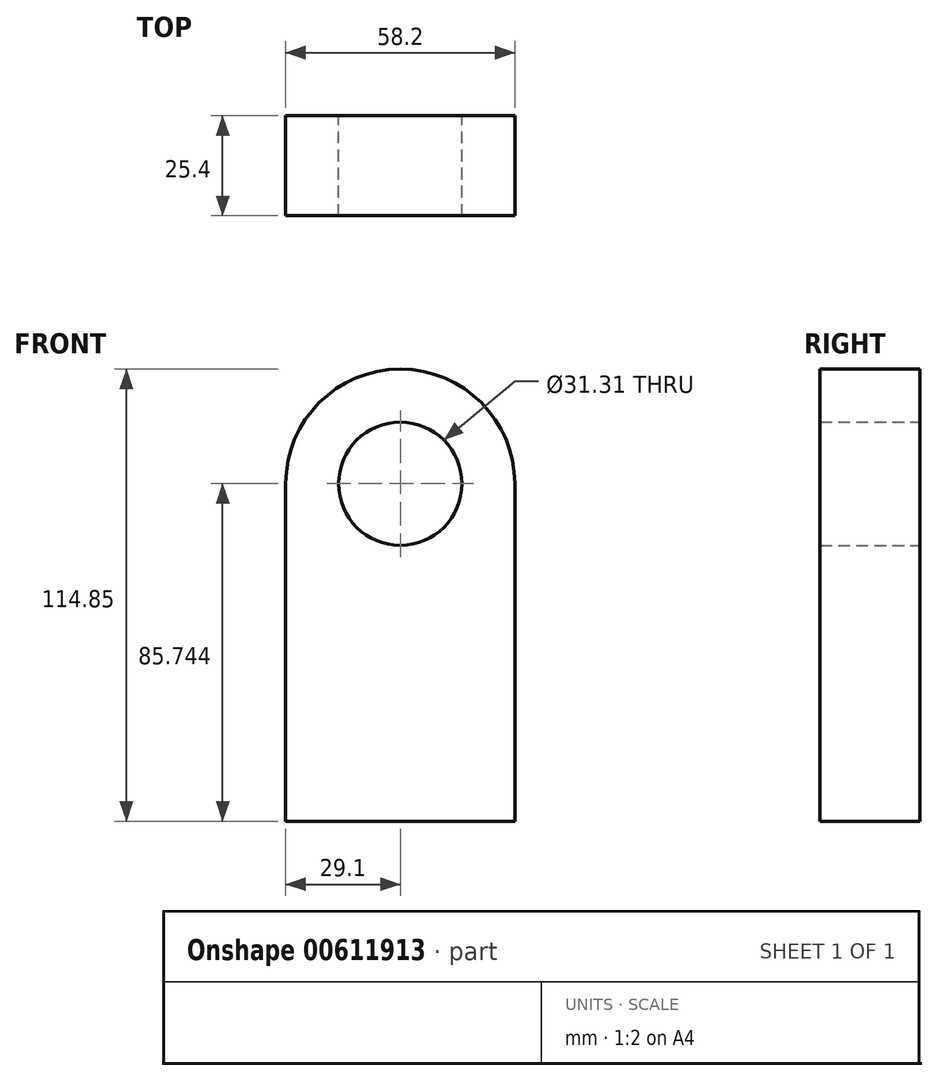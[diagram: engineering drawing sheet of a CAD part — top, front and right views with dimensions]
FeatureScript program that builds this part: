
annotation { "Feature Type Name" : "Feature", "Feature Type Description" : "" }
export const myFeature = defineFeature(function(context is Context, id is Id, definition is map)
    precondition{}
    {
        {
            var Q0;
            Q0=qCreatedBy(makeId("Front.planeOp"),FACE);
            var sketch = newSketch(context, id + "F0", { "sketchPlane" : qUnion([Q0])});
            skLineSegment(sketch, "E0.top", {"start": v(-29.1, -42.87) * mm, "end": v(29.1, -42.87) * mm});
            skLineSegment(sketch, "E0.left", {"start": v(-29.1, 42.87) * mm, "end": v(-29.1, -42.87) * mm});
            skLineSegment(sketch, "E0.right", {"start": v(29.1, 42.87) * mm, "end": v(29.1, -42.87) * mm});
            skPoint(sketch, "E0.middle", {"position": v(0, 0) * mm});
            skArc(sketch, "E1", {"start": v(29.1, 42.87) * mm, "mid": v(0, 71.98) * mm, "end": v(-29.1, 42.87) * mm});
            skCircle(sketch, "E2", {"center": v(0, 42.87) * mm, "radius": 15.66 * mm});
            skSolve(sketch);
        }
        {
            var Q0;
            Q0 = qSketchRegion(id + "F0", true);
            extrude(context, id + "F1", {"entities" : qUnion([Q0]), "depth" : 25.4 * mm, "offsetDistance" : 25.4 * mm});
        }
    });
